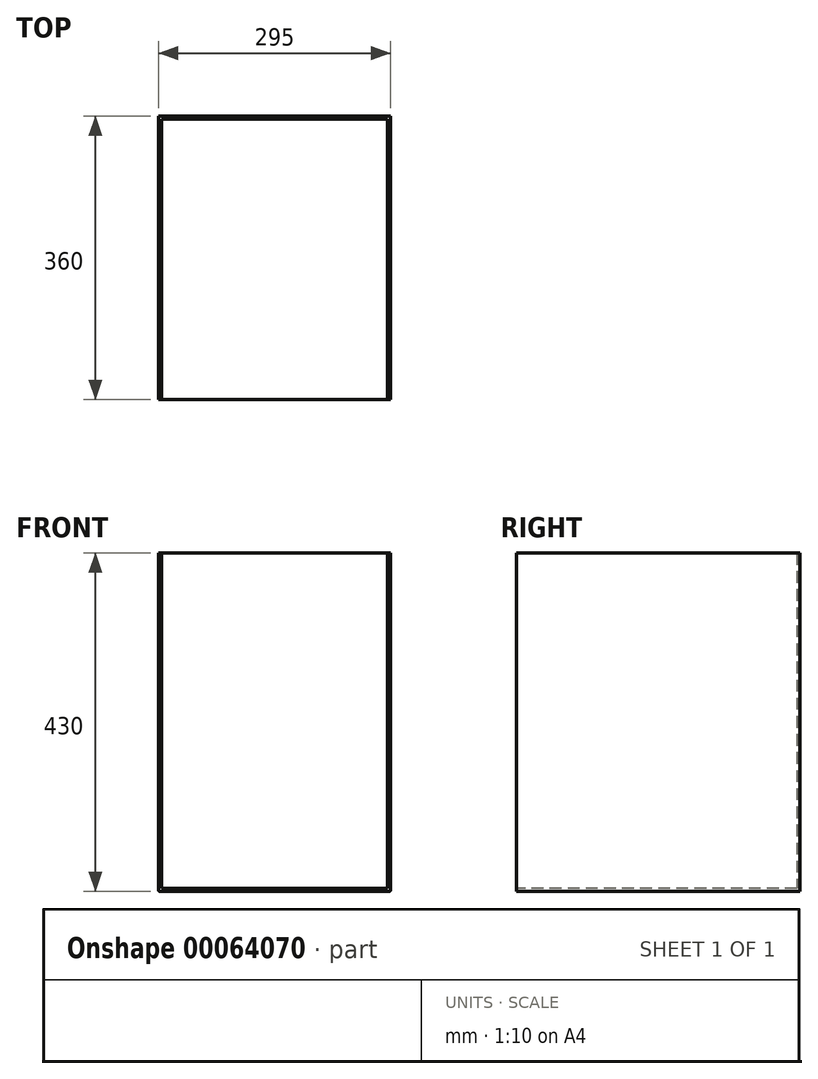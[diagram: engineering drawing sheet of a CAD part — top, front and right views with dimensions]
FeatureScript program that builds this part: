
annotation { "Feature Type Name" : "Feature", "Feature Type Description" : "" }
export const myFeature = defineFeature(function(context is Context, id is Id, definition is map)
    precondition{}
    {
        {
            var Q0;
            Q0=qCreatedBy(makeId("Top.planeOp"),FACE);
            var sketch = newSketch(context, id + "F0", { "sketchPlane" : qUnion([Q0])});
            skLineSegment(sketch, "E0", {"start": v(0, -360) * mm, "end": v(0, 0) * mm});
            skLineSegment(sketch, "E1.MirrorCS", {"start": v(-4, -360) * mm, "end": v(-4, -4) * mm});
            skLineSegment(sketch, "E2.MirrorCS", {"start": v(-4, -4) * mm, "end": v(-291, -4) * mm});
            skLineSegment(sketch, "E3.MirrorCS", {"start": v(0, 0) * mm, "end": v(-295, 0) * mm});
            skLineSegment(sketch, "E4.MirrorCS", {"start": v(-295, 0) * mm, "end": v(-295, -360) * mm});
            skLineSegment(sketch, "E5.MirrorCS", {"start": v(-291, -4) * mm, "end": v(-291, -360) * mm});
            skLineSegment(sketch, "E6.MirrorCS", {"start": v(-291, -360) * mm, "end": v(-295, -360) * mm});
            skLineSegment(sketch, "E7", {"start": v(0, -360) * mm, "end": v(-4, -360) * mm});
            skSolve(sketch);
        }
        {
            var Q0;
            Q0=makeQuery(id+"F0.imprint","IMPRINT",FACE,{"disambiguationData":[TD([[makeQuery(id+"F0.imprint","IMPRINT",EDGE,{"derivedFrom":sQuery(id+"F0.wireOp",EDGE,"8549452f-c1c4-4c66-b43a-6f4cb653c117")}),-1.0]])]});
            var Q1;
            Q1=makeQuery(id+"F0.imprint","IMPRINT",FACE,{"disambiguationData":[TD([[makeQuery(id+"F0.imprint","IMPRINT",EDGE,{"derivedFrom":sQuery(id+"F0.wireOp",EDGE,"E0")}),1.0]])]});
            extrude(context, id + "F1", {"entities" : qUnion([Q0, Q1]), "depth" : 426 * mm});
        }
        {
            var Q0;
            Q0=qCreatedBy(makeId("Top.planeOp"),FACE);
            var sketch = newSketch(context, id + "F2", { "sketchPlane" : qUnion([Q0])});
            skLineSegment(sketch, "E8.bottom", {"start": v(0, 0) * mm, "end": v(-295, 0) * mm});
            skLineSegment(sketch, "E8.top", {"start": v(0, -360) * mm, "end": v(-295, -360) * mm});
            skLineSegment(sketch, "E8.left", {"start": v(0, 0) * mm, "end": v(0, -360) * mm});
            skLineSegment(sketch, "E8.right", {"start": v(-295, 0) * mm, "end": v(-295, -360) * mm});
            skSolve(sketch);
        }
        {
            var Q0;
            Q0=qSketchRegion(id+"F2",true);
            extrude(context, id + "F3", {"entities" : qUnion([Q0]), "operationType" : NewBodyOperationType.ADD, "oppositeDirection" : true, "depth" : 4 * mm});
        }
        {
            var Q0;
            Q0=makeQuery(id+"F3.opExtrude","CAP_EDGE",EDGE,{"disambiguationData":[OSD([sQuery(id+"F2.wireOp",EDGE,"vbA2sRL1-BuKc-cXEJ-8hRA-xlI7hLZ0s6HN")])],"isStart":false});
            var Q1;
            Q1=makeQuery(id+"F3.opExtrude","CAP_EDGE",EDGE,{"disambiguationData":[OSD([sQuery(id+"F2.wireOp",EDGE,"271fb2c7-7bc5-40ae-a16a-63b087808d34.0")])],"isStart":false});
            var Q2;
            Q2=makeQuery(id+"F3.opExtrude","CAP_EDGE",EDGE,{"disambiguationData":[OSD([sQuery(id+"F2.wireOp",EDGE,"7babfaa8-3942-4671-b239-a5d87d0b72e7.0")])],"isStart":false});
            var Q3;
            Q3=makeQuery(id+"F3.opExtrude","CAP_EDGE",EDGE,{"disambiguationData":[OSD([sQuery(id+"F2.wireOp",EDGE,"E8.right")])],"isStart":false});
            var Q4;
            Q4=makeQuery(id+"F3.opExtrude","CAP_EDGE",EDGE,{"disambiguationData":[OSD([sQuery(id+"F2.wireOp",EDGE,"E8.left")])],"isStart":false});
            fillet(context, id + "F4", {"entities" : qUnion([Q0, Q1, Q2, Q3, Q4]), "radius" : 2 * mm, "tangentPropagation" : true, "allowEdgeOverflow" : false});
        }
    });
